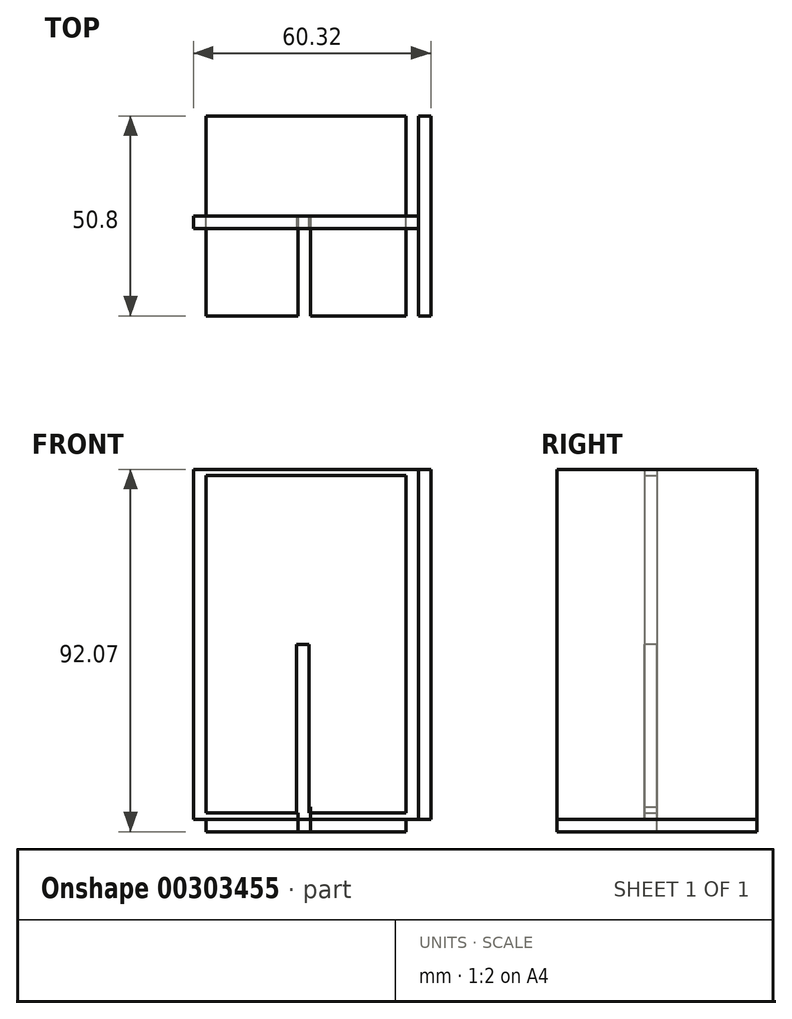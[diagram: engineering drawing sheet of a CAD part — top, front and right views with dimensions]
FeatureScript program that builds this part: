
annotation { "Feature Type Name" : "Feature", "Feature Type Description" : "" }
export const myFeature = defineFeature(function(context is Context, id is Id, definition is map)
    precondition{}
    {
        {
            var Q0;
            Q0=qCreatedBy(makeId("Front.planeOp"),FACE);
            var sketch = newSketch(context, id + "F0", { "sketchPlane" : qUnion([Q0])});
            skLineSegment(sketch, "E0.bottom", {"start": v(-28.57, 44.45) * mm, "end": v(28.58, 44.45) * mm});
            skLineSegment(sketch, "E0.top", {"start": v(-28.58, -44.45) * mm, "end": v(28.58, -44.45) * mm});
            skLineSegment(sketch, "E0.left", {"start": v(-28.57, 44.45) * mm, "end": v(-28.58, -44.45) * mm});
            skLineSegment(sketch, "E0.right", {"start": v(28.58, 44.45) * mm, "end": v(28.58, -44.45) * mm});
            skPoint(sketch, "E0.middle", {"position": v(0, 0) * mm});
            skSolve(sketch);
        }
        {
            var Q0;
            Q0 = qSketchRegion(id + "F0", true);
            extrude(context, id + "F1", {"entities" : qUnion([Q0]), "depth" : 3.17 * mm});
        }
        {
            var Q0;
            Q0=makeQuery(id+"F1.opExtrude","SWEPT_FACE",FACE,{"disambiguationData":[OSD([sQuery(id+"F0.wireOp",EDGE,"E0.right")])]});
            var sketch = newSketch(context, id + "F2", { "sketchPlane" : qUnion([Q0])});
            skLineSegment(sketch, "E1.bottom", {"start": v(25.4, 44.45) * mm, "end": v(-25.4, 44.45) * mm});
            skLineSegment(sketch, "E1.top", {"start": v(25.4, -44.45) * mm, "end": v(-25.4, -44.45) * mm});
            skLineSegment(sketch, "E1.left", {"start": v(25.4, 44.45) * mm, "end": v(25.4, -44.45) * mm});
            skLineSegment(sketch, "E1.right", {"start": v(-25.4, 44.45) * mm, "end": v(-25.4, -44.45) * mm});
            skPoint(sketch, "E1.middle", {"position": v(0, 0) * mm});
            skSolve(sketch);
        }
        {
            var Q0;
            Q0 = qSketchRegion(id + "F2", true);
            extrude(context, id + "F3", {"entities" : qUnion([Q0]), "depth" : 3.17 * mm});
        }
        {
            var Q0;
            Q0=makeQuery(id+"F3.opExtrude","SWEPT_FACE",FACE,{"disambiguationData":[OSD([sQuery(id+"F2.wireOp",EDGE,"E1.top")])]});
            var sketch = newSketch(context, id + "F4", { "sketchPlane" : qUnion([Q0])});
            skLineSegment(sketch, "E2.bottom", {"start": v(25.4, 25.4) * mm, "end": v(-25.4, 25.4) * mm});
            skLineSegment(sketch, "E2.top", {"start": v(25.4, -25.4) * mm, "end": v(-25.4, -25.4) * mm});
            skLineSegment(sketch, "E2.left", {"start": v(25.4, 25.4) * mm, "end": v(25.4, -25.4) * mm});
            skLineSegment(sketch, "E2.right", {"start": v(-25.4, 25.4) * mm, "end": v(-25.4, -25.4) * mm});
            skPoint(sketch, "E2.middle", {"position": v(0, 0) * mm});
            skSolve(sketch);
        }
        {
            var Q0;
            Q0 = qSketchRegion(id + "F4", true);
            extrude(context, id + "F5", {"entities" : qUnion([Q0]), "depth" : 3.17 * mm});
        }
        {
            var Q0;
            Q0=makeQuery(id+"F5.opExtrude","CAP_FACE",FACE,{"disambiguationData":[OSD([sQuery(id+"F4.wireOp",EDGE,"E2.bottom"),sQuery(id+"F4.wireOp",EDGE,"E2.top"),sQuery(id+"F4.wireOp",EDGE,"E2.left"),sQuery(id+"F4.wireOp",EDGE,"E2.right")])],"isStart":true});
            var sketch = newSketch(context, id + "F6", { "sketchPlane" : qUnion([Q0])});
            skLineSegment(sketch, "E3.bottom", {"start": v(-25.4, 42.86) * mm, "end": v(25.4, 42.86) * mm});
            skLineSegment(sketch, "E3.top", {"start": v(-25.4, -42.86) * mm, "end": v(25.4, -42.86) * mm});
            skLineSegment(sketch, "E3.left", {"start": v(-25.4, 42.86) * mm, "end": v(-25.4, -42.86) * mm});
            skLineSegment(sketch, "E3.right", {"start": v(25.4, 42.86) * mm, "end": v(25.4, -42.86) * mm});
            skLineSegment(sketch, "E4.top", {"start": v(0, -42.86) * mm, "end": v(0, -42.86) * mm});
            skLineSegment(sketch, "E5.bottom", {"start": v(0, 0) * mm, "end": v(0, 0) * mm});
            skLineSegment(sketch, "E5.top", {"start": v(0.37, -42.86) * mm, "end": v(0.37, -42.86) * mm});
            skSolve(sketch);
        }
        {
            var Q0;
            Q0 = qSketchRegion(id + "F6", true);
            extrude(context, id + "F7", {"entities" : qUnion([Q0]), "depth" : 3.17 * mm});
        }
        {
            var Q0;
            Q0=makeQuery(id+"F7.opExtrude","CAP_FACE",FACE,{"disambiguationData":[OSD([sQuery(id+"F6.wireOp",EDGE,"E3.bottom"),sQuery(id+"F6.wireOp",EDGE,"E3.top"),sQuery(id+"F6.wireOp",EDGE,"E3.left"),sQuery(id+"F6.wireOp",EDGE,"E3.right")])],"isStart":false});
            var sketch = newSketch(context, id + "F8", { "sketchPlane" : qUnion([Q0])});
            skLineSegment(sketch, "E6.bottom", {"start": v(1.14, -42.86) * mm, "end": v(-2.04, -42.86) * mm});
            skLineSegment(sketch, "E6.top", {"start": v(1.14, 0) * mm, "end": v(-2.04, 0) * mm});
            skLineSegment(sketch, "E6.left", {"start": v(1.14, -42.86) * mm, "end": v(1.14, 0) * mm});
            skLineSegment(sketch, "E6.right", {"start": v(-2.04, -42.86) * mm, "end": v(-2.04, 0) * mm});
            skSolve(sketch);
        }
        {
            var Q0;
            Q0 = qSketchRegion(id + "F8", true);
            extrude(context, id + "F9", {"entities" : qUnion([Q0]), "operationType" : NewBodyOperationType.REMOVE, "oppositeDirection" : true, "depth" : 25.4 * mm});
        }
        {
            var Q0;
            Q0=makeQuery(id+"F0.imprint","IMPRINT",FACE,{"disambiguationData":[TD([[makeQuery(id+"F0.imprint","IMPRINT",EDGE,{"derivedFrom":sQuery(id+"F0.wireOp",EDGE,"E0.bottom")}),-1.0]])]});
            var sketch = newSketch(context, id + "F10", { "sketchPlane" : qUnion([Q0])});
            skLineSegment(sketch, "E7.bottom", {"start": v(-25.4, 42.86) * mm, "end": v(25.4, 42.86) * mm});
            skLineSegment(sketch, "E7.top", {"start": v(-25.4, -42.86) * mm, "end": v(25.4, -42.86) * mm});
            skLineSegment(sketch, "E7.left", {"start": v(-25.4, 42.86) * mm, "end": v(-25.4, -42.86) * mm});
            skLineSegment(sketch, "E7.right", {"start": v(25.4, 42.86) * mm, "end": v(25.4, -42.86) * mm});
            skPoint(sketch, "E7.middle", {"position": v(0, 0) * mm});
            skSolve(sketch);
        }
        {
            var Q0;
            Q0 = qSketchRegion(id + "F10", true);
            extrude(context, id + "F11", {"entities" : qUnion([Q0]), "depth" : 3.17 * mm});
        }
        {
            var Q0;
            Q0=makeQuery(id+"F11.opExtrude","CAP_FACE",FACE,{"disambiguationData":[OSD([sQuery(id+"F10.wireOp",EDGE,"E7.bottom"),sQuery(id+"F10.wireOp",EDGE,"E7.top"),sQuery(id+"F10.wireOp",EDGE,"E7.left"),sQuery(id+"F10.wireOp",EDGE,"E7.right")])],"isStart":false});
            var sketch = newSketch(context, id + "F12", { "sketchPlane" : qUnion([Q0])});
            skLineSegment(sketch, "E8.bottom", {"start": v(0.8, -42.86) * mm, "end": v(-2.37, -42.86) * mm});
            skLineSegment(sketch, "E8.top", {"start": v(0.8, 0) * mm, "end": v(-2.37, 0) * mm});
            skLineSegment(sketch, "E8.left", {"start": v(0.8, -42.86) * mm, "end": v(0.8, 0) * mm});
            skLineSegment(sketch, "E8.right", {"start": v(-2.37, -42.86) * mm, "end": v(-2.37, 0) * mm});
            skSolve(sketch);
        }
        {
            var Q0;
            Q0 = qSketchRegion(id + "F12", true);
            extrude(context, id + "F13", {"entities" : qUnion([Q0]), "operationType" : NewBodyOperationType.REMOVE, "oppositeDirection" : true, "depth" : 25.4 * mm});
        }
        {
            var Q0;
            Q0=makeQuery(id+"F7.opExtrude","SWEPT_BODY",BODY,{"disambiguationData":[OSD([sQuery(id+"F6.wireOp",EDGE,"E3.bottom"),sQuery(id+"F6.wireOp",EDGE,"E3.top"),sQuery(id+"F6.wireOp",EDGE,"E3.left"),sQuery(id+"F6.wireOp",EDGE,"E3.right")])]});
            deleteBodies(context, id + "F14", {"entities" : qUnion([Q0])});
        }
    });
